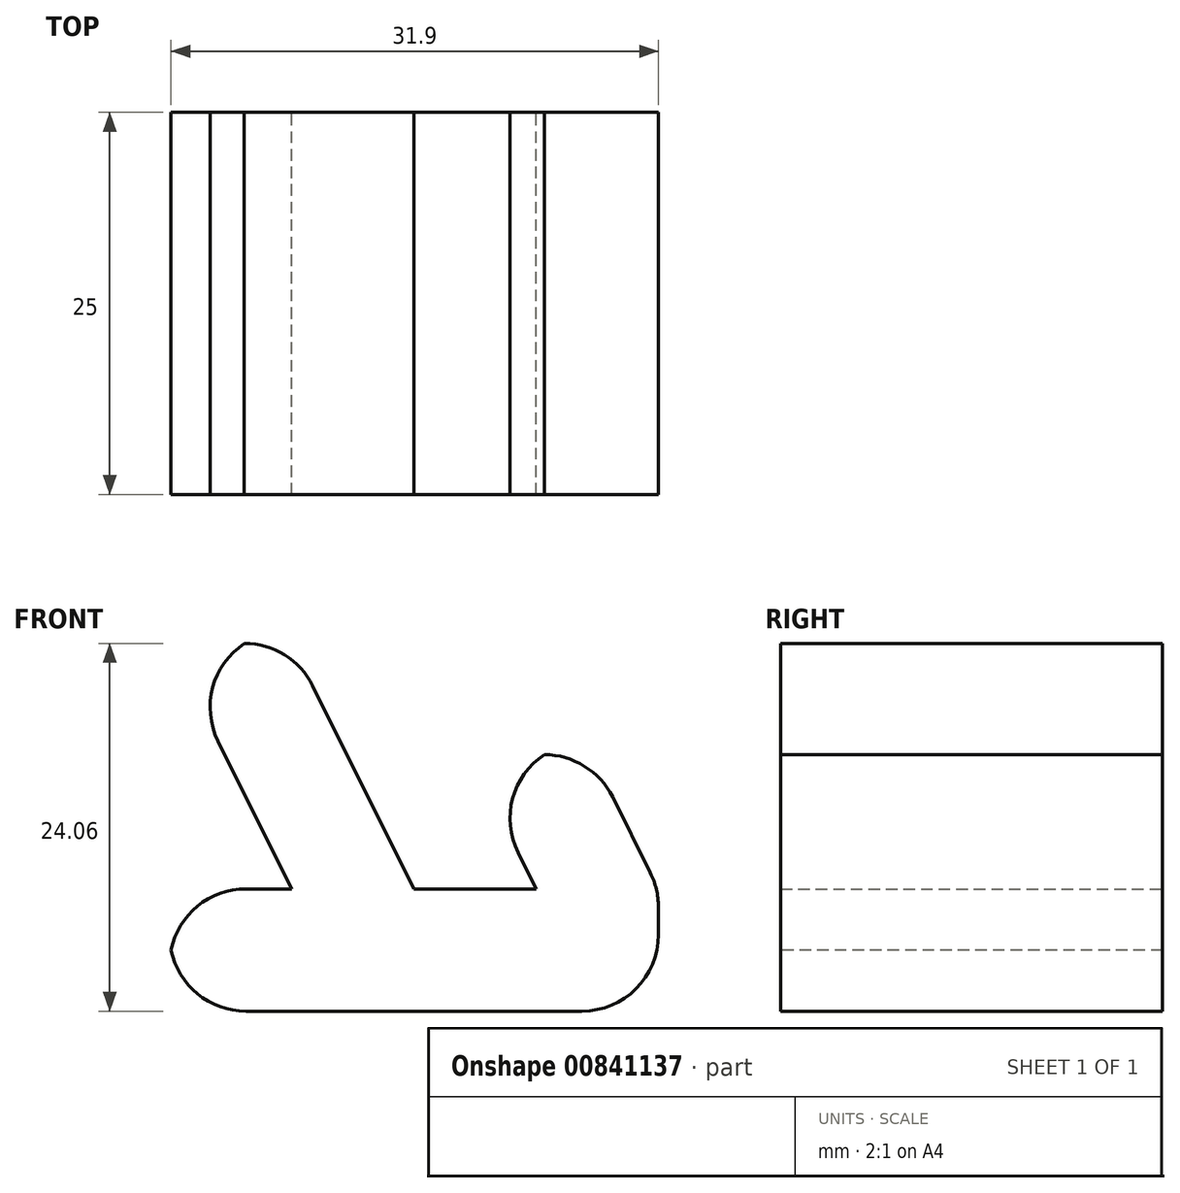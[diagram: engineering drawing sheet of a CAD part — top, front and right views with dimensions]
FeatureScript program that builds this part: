
annotation { "Feature Type Name" : "Feature", "Feature Type Description" : "" }
export const myFeature = defineFeature(function(context is Context, id is Id, definition is map)
    precondition{}
    {
        {
            var Q0;
            Q0=qCreatedBy(makeId("Front.planeOp"),FACE);
            var sketch = newSketch(context, id + "F0", { "sketchPlane" : qUnion([Q0])});
            skLineSegment(sketch, "E0.bottom", {"start": v(16, -4) * mm, "end": v(-16, -4) * mm});
            skLineSegment(sketch, "E0.top", {"start": v(16, 4) * mm, "end": v(-16, 4) * mm});
            skLineSegment(sketch, "E0.left", {"start": v(16, -4) * mm, "end": v(16, 4) * mm});
            skLineSegment(sketch, "E0.right", {"start": v(-16, -4) * mm, "end": v(-16, 4) * mm});
            skPoint(sketch, "E0.middle", {"position": v(0, 0) * mm});
            skLineSegment(sketch, "E1", {"start": v(16, 4) * mm, "end": v(11.63, 12.78) * mm});
            skLineSegment(sketch, "E2", {"start": v(11.63, 12.78) * mm, "end": v(3.63, 12.78) * mm});
            skLineSegment(sketch, "E3", {"start": v(3.63, 12.78) * mm, "end": v(8, 4) * mm});
            skLineSegment(sketch, "E4", {"start": v(0, 4) * mm, "end": v(-8, 20.06) * mm});
            skLineSegment(sketch, "E5", {"start": v(-8, 20.06) * mm, "end": v(-16, 20.06) * mm});
            skLineSegment(sketch, "E6", {"start": v(-16, 20.06) * mm, "end": v(-8, 4) * mm});
            skSolve(sketch);
        }
        {
            var Q0;
            Q0 = qSketchRegion(id + "F0", true);
            extrude(context, id + "F1", {"entities" : qUnion([Q0]), "depth" : 25 * mm, "offsetDistance" : 25 * mm});
        }
        {
            var Q0;
            Q0=makeQuery(id+"F1.opExtrude","SWEPT_EDGE",EDGE,{"disambiguationData":[OSD([sQuery(id+"F0.wireOp",EDGE,"E4"),sQuery(id+"F0.wireOp",EDGE,"E5")])]});
            var Q1;
            Q1=makeQuery(id+"F1.opExtrude","SWEPT_EDGE",EDGE,{"disambiguationData":[OSD([sQuery(id+"F0.wireOp",EDGE,"E1"),sQuery(id+"F0.wireOp",EDGE,"E2")])]});
            var Q2;
            Q2=makeQuery(id+"F1.opExtrude","SWEPT_EDGE",EDGE,{"disambiguationData":[OSD([sQuery(id+"F0.wireOp",EDGE,"E0.top"),sQuery(id+"F0.wireOp",EDGE,"E0.left"),sQuery(id+"F0.wireOp",EDGE,"E1")])]});
            fillet(context, id + "F2", {"entities" : qUnion([Q0, Q1, Q2]), "radius" : 5 * mm, "tangentPropagation" : true, "allowEdgeOverflow" : false});
        }
        {
            var Q0;
            Q0=makeQuery(id+"F1.opExtrude","SWEPT_EDGE",EDGE,{"disambiguationData":[OSD([sQuery(id+"F0.wireOp",EDGE,"E2"),sQuery(id+"F0.wireOp",EDGE,"E3")])]});
            var Q1;
            Q1=makeQuery(id+"F1.opExtrude","SWEPT_EDGE",EDGE,{"disambiguationData":[OSD([sQuery(id+"F0.wireOp",EDGE,"E5"),sQuery(id+"F0.wireOp",EDGE,"E6")])]});
            var Q2;
            Q2=makeQuery(id+"F1.opExtrude","SWEPT_EDGE",EDGE,{"disambiguationData":[OSD([sQuery(id+"F0.wireOp",EDGE,"E0.top"),sQuery(id+"F0.wireOp",EDGE,"E0.right")])]});
            var Q3;
            Q3=makeQuery(id+"F1.opExtrude","SWEPT_EDGE",EDGE,{"disambiguationData":[OSD([sQuery(id+"F0.wireOp",EDGE,"E0.bottom"),sQuery(id+"F0.wireOp",EDGE,"E0.right")])]});
            fillet(context, id + "F3", {"entities" : qUnion([Q0, Q1, Q2, Q3]), "radius" : 5 * mm, "tangentPropagation" : true, "allowEdgeOverflow" : false});
        }
        {
            var Q0;
            Q0=makeQuery(id+"F1.opExtrude","SWEPT_EDGE",EDGE,{"disambiguationData":[OSD([sQuery(id+"F0.wireOp",EDGE,"E0.bottom"),sQuery(id+"F0.wireOp",EDGE,"E0.left")])]});
            fillet(context, id + "F4", {"entities" : qUnion([Q0]), "radius" : 5 * mm, "tangentPropagation" : true, "allowEdgeOverflow" : false});
        }
    });
